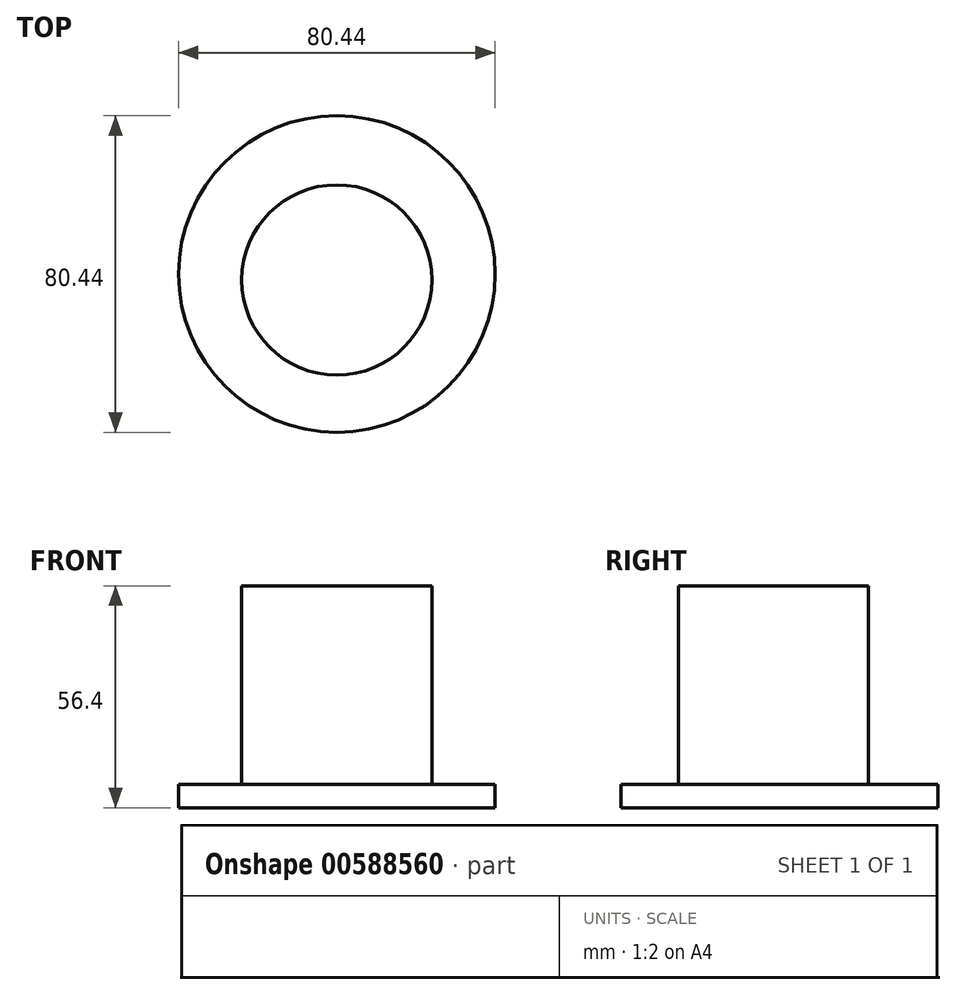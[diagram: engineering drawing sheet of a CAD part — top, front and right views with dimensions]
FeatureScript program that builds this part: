
annotation { "Feature Type Name" : "Feature", "Feature Type Description" : "" }
export const myFeature = defineFeature(function(context is Context, id is Id, definition is map)
    precondition{}
    {
        {
            var Q0;
            Q0=qCreatedBy(makeId("Top.planeOp"),FACE);
            var sketch = newSketch(context, id + "F0", { "sketchPlane" : qUnion([Q0])});
            skCircle(sketch, "E0", {"center": v(0, 0) * mm, "radius": 40.22 * mm});
            skSolve(sketch);
        }
        {
            var Q0;
            Q0 = qSketchRegion(id + "F0", true);
            extrude(context, id + "F1", {"entities" : qUnion([Q0]), "depth" : 6 * mm, "offsetDistance" : 25 * mm});
        }
        {
            var Q0;
            Q0=qCreatedBy(makeId("Top.planeOp"),FACE);
            var sketch = newSketch(context, id + "F2", { "sketchPlane" : qUnion([Q0])});
            skCircle(sketch, "E1", {"center": v(0, -1.51) * mm, "radius": 24.17 * mm});
            skSolve(sketch);
        }
        {
            var Q0;
            Q0=makeQuery(id+"F2.imprint","IMPRINT",FACE,{"disambiguationData":[TD([[makeQuery(id+"F2.imprint","IMPRINT",EDGE,{"derivedFrom":sQuery(id+"F2.wireOp",EDGE,"E1")}),1.0]])]});
            extrude(context, id + "F3", {"entities" : qUnion([Q0]), "operationType" : NewBodyOperationType.ADD, "depth" : 56.4 * mm, "offsetDistance" : 25 * mm});
        }
    });
